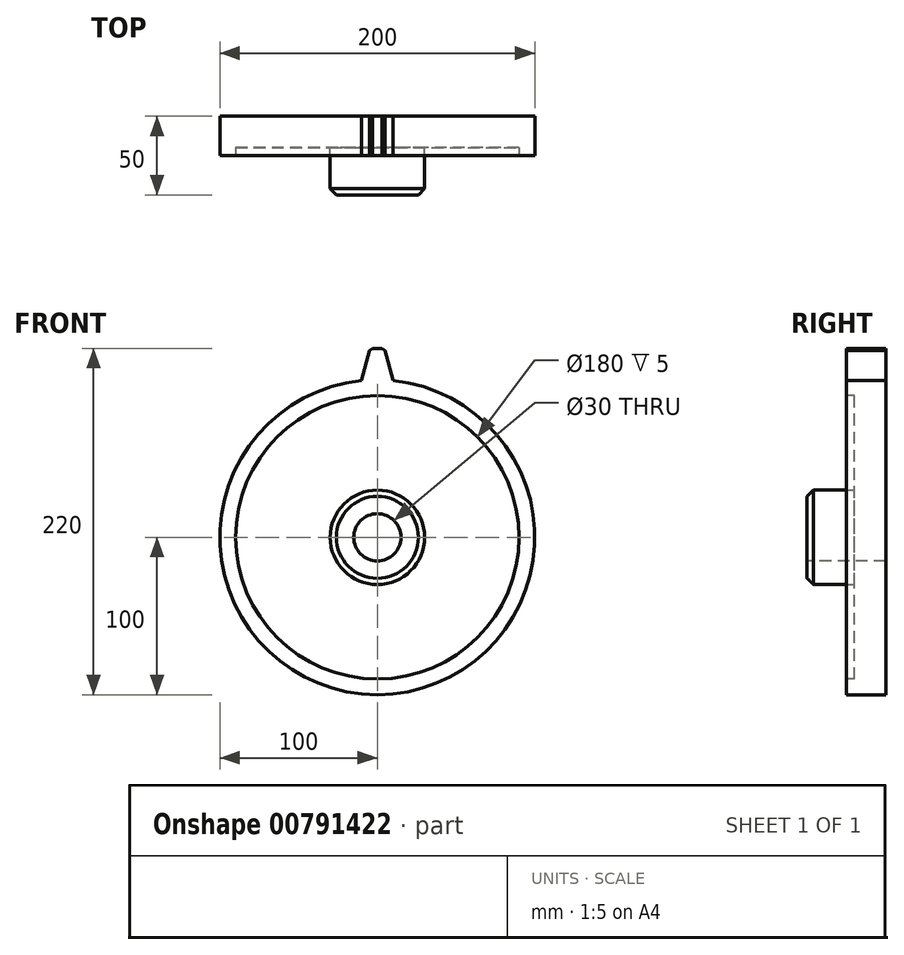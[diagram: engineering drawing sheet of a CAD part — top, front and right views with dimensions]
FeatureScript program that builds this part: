
annotation { "Feature Type Name" : "Feature", "Feature Type Description" : "" }
export const myFeature = defineFeature(function(context is Context, id is Id, definition is map)
    precondition{}
    {
        {
            var Q0;
            Q0=qCreatedBy(makeId("Front.planeOp"),FACE);
            var sketch = newSketch(context, id + "F0", { "sketchPlane" : qUnion([Q0])});
            skCircle(sketch, "E0", {"center": v(0, 0) * mm, "radius": 100 * mm});
            skSolve(sketch);
        }
        {
            var Q0;
            Q0=makeQuery(id+"F0.imprint","IMPRINT",FACE,{"disambiguationData":[TD([[makeQuery(id+"F0.imprint","IMPRINT",EDGE,{"derivedFrom":sQuery(id+"F0.wireOp",EDGE,"E0")}),1.0]])]});
            var Q1;
            Q1 = qSketchRegion(id + "F6", true);
            extrude(context, id + "F1", {"entities" : qUnion([Q0, Q1]), "depth" : 25 * mm, "offsetDistance" : 25 * mm});
        }
        {
            var Q0;
            Q0=makeQuery(id+"F1.opExtrude","CAP_FACE",FACE,{"disambiguationData":[OSD([sQuery(id+"F0.wireOp",EDGE,"E0")])],"isStart":false});
            var sketch = newSketch(context, id + "F2", { "sketchPlane" : qUnion([Q0])});
            skLineSegment(sketch, "E1", {"start": v(-10, 99.5) * mm, "end": v(10, 99.5) * mm});
            skLineSegment(sketch, "E2", {"start": v(10, 99.5) * mm, "end": v(4.5, 120) * mm});
            skLineSegment(sketch, "E3", {"start": v(4.5, 120) * mm, "end": v(-4.5, 120) * mm});
            skLineSegment(sketch, "E4", {"start": v(-4.5, 120) * mm, "end": v(-10, 99.5) * mm});
            skSolve(sketch);
        }
        {
            var Q0;
            {var subQ0=sQuery(id+"F2.wireOp",EDGE,"E2");Q0=makeQuery(id+"F2.imprint","IMPRINT",FACE,{"disambiguationData":[TD([[makeQuery(id+"F2.imprint","IMPRINT",EDGE,{"derivedFrom":subQ0}),1.0]])]});}
            var Q1;
            Q1=makeQuery(id+"F1.opExtrude","CAP_FACE",FACE,{"disambiguationData":[OSD([sQuery(id+"F0.wireOp",EDGE,"E0")])],"isStart":true});
            extrude(context, id + "F3", {"entities" : qUnion([Q0]), "operationType" : NewBodyOperationType.ADD, "endBound" : BoundingType.UP_TO_SURFACE, "oppositeDirection" : true, "depth" : 25 * mm, "endBoundEntityFace" : qUnion([Q1]), "offsetDistance" : 25 * mm});
        }
        {
            var Q0;
            Q0=makeQuery(id+"F3.opExtrude","SWEPT_EDGE",EDGE,{"disambiguationData":[OSD([sQuery(id+"F0.wireOp",EDGE,"E0"),sQuery(id+"F2.wireOp",EDGE,"E1"),sQuery(id+"F2.wireOp",EDGE,"E2")])]});
            var Q1;
            Q1=makeQuery(id+"F3.opExtrude","SWEPT_EDGE",EDGE,{"disambiguationData":[OSD([sQuery(id+"F0.wireOp",EDGE,"E0"),sQuery(id+"F2.wireOp",EDGE,"E1"),sQuery(id+"F2.wireOp",EDGE,"E4")])]});
            fillet(context, id + "F4", {"entities" : qUnion([Q0, Q1]), "radius" : 5 * mm, "tangentPropagation" : true, "allowEdgeOverflow" : false});
        }
        {
            var Q0;
            Q0=makeQuery(id+"F3.opExtrude","SWEPT_EDGE",EDGE,{"disambiguationData":[OSD([sQuery(id+"F2.wireOp",EDGE,"E2"),sQuery(id+"F2.wireOp",EDGE,"E3")])]});
            var Q1;
            Q1=makeQuery(id+"F3.opExtrude","SWEPT_EDGE",EDGE,{"disambiguationData":[OSD([sQuery(id+"F2.wireOp",EDGE,"E3"),sQuery(id+"F2.wireOp",EDGE,"E4")])]});
            chamfer(context, id + "F5", {"entities" : qUnion([Q0, Q1]), "width" : 2 * mm, "tangentPropagation" : true});
        }
        {
            var Q0;
            {var subQ0=sQuery(id+"F2.wireOp",EDGE,"E4");var subQ1=sQuery(id+"F2.wireOp",EDGE,"E3");var subQ2=sQuery(id+"F2.wireOp",EDGE,"E2");var subQ3=sQuery(id+"F0.wireOp",EDGE,"E0");Q0=makeQuery(id+"FVngeMlJqadk3JX_1.19.F3.boolean.opBoolean","MERGE",FACE,{"derivedFrom":[makeQuery(id+"FVngeMlJqadk3JX_1.18.F3.boolean.opBoolean","MERGE",FACE,{"derivedFrom":[makeQuery(id+"FVngeMlJqadk3JX_1.17.F3.boolean.opBoolean","MERGE",FACE,{"derivedFrom":[makeQuery(id+"FVngeMlJqadk3JX_1.16.F3.boolean.opBoolean","MERGE",FACE,{"derivedFrom":[makeQuery(id+"FVngeMlJqadk3JX_1.15.F3.boolean.opBoolean","MERGE",FACE,{"derivedFrom":[makeQuery(id+"FVngeMlJqadk3JX_1.14.F3.boolean.opBoolean","MERGE",FACE,{"derivedFrom":[makeQuery(id+"FVngeMlJqadk3JX_1.13.F3.boolean.opBoolean","MERGE",FACE,{"derivedFrom":[makeQuery(id+"FVngeMlJqadk3JX_1.12.F3.boolean.opBoolean","MERGE",FACE,{"derivedFrom":[makeQuery(id+"FVngeMlJqadk3JX_1.11.F3.boolean.opBoolean","MERGE",FACE,{"derivedFrom":[makeQuery(id+"FVngeMlJqadk3JX_1.10.F3.boolean.opBoolean","MERGE",FACE,{"derivedFrom":[makeQuery(id+"FVngeMlJqadk3JX_1.9.F3.boolean.opBoolean","MERGE",FACE,{"derivedFrom":[makeQuery(id+"FVngeMlJqadk3JX_1.8.F3.boolean.opBoolean","MERGE",FACE,{"derivedFrom":[makeQuery(id+"FVngeMlJqadk3JX_1.7.F3.boolean.opBoolean","MERGE",FACE,{"derivedFrom":[makeQuery(id+"FVngeMlJqadk3JX_1.6.F3.boolean.opBoolean","MERGE",FACE,{"derivedFrom":[makeQuery(id+"FVngeMlJqadk3JX_1.5.F3.boolean.opBoolean","MERGE",FACE,{"derivedFrom":[makeQuery(id+"FVngeMlJqadk3JX_1.4.F3.boolean.opBoolean","MERGE",FACE,{"derivedFrom":[makeQuery(id+"FVngeMlJqadk3JX_1.3.F3.boolean.opBoolean","MERGE",FACE,{"derivedFrom":[makeQuery(id+"FVngeMlJqadk3JX_1.2.F3.boolean.opBoolean","MERGE",FACE,{"derivedFrom":[makeQuery(id+"FVngeMlJqadk3JX_1.1.F3.boolean.opBoolean","MERGE",FACE,{"derivedFrom":[makeQuery(id+"F3.boolean.opBoolean","MERGE",FACE,{"derivedFrom":[makeQuery(id+"F1.opExtrude","CAP_FACE",FACE,{"disambiguationData":[OSD([subQ3])],"isStart":false}),makeQuery(id+"F3.opExtrude","CAP_FACE",FACE,{"disambiguationData":[OSD([subQ3,subQ2,subQ1,subQ0])],"isStart":true})]}),makeQuery(id+"FVngeMlJqadk3JX_1.1.F3.opExtrude","CAP_FACE",FACE,{"disambiguationData":[OSD([subQ3,subQ2,subQ1,subQ0])],"isStart":true})]}),makeQuery(id+"FVngeMlJqadk3JX_1.2.F3.opExtrude","CAP_FACE",FACE,{"disambiguationData":[OSD([subQ3,subQ2,subQ1,subQ0])],"isStart":true})]}),makeQuery(id+"FVngeMlJqadk3JX_1.3.F3.opExtrude","CAP_FACE",FACE,{"disambiguationData":[OSD([subQ3,subQ2,subQ1,subQ0])],"isStart":true})]}),makeQuery(id+"FVngeMlJqadk3JX_1.4.F3.opExtrude","CAP_FACE",FACE,{"disambiguationData":[OSD([subQ3,subQ2,subQ1,subQ0])],"isStart":true})]}),makeQuery(id+"FVngeMlJqadk3JX_1.5.F3.opExtrude","CAP_FACE",FACE,{"disambiguationData":[OSD([subQ3,subQ2,subQ1,subQ0])],"isStart":true})]}),makeQuery(id+"FVngeMlJqadk3JX_1.6.F3.opExtrude","CAP_FACE",FACE,{"disambiguationData":[OSD([subQ3,subQ2,subQ1,subQ0])],"isStart":true})]}),makeQuery(id+"FVngeMlJqadk3JX_1.7.F3.opExtrude","CAP_FACE",FACE,{"disambiguationData":[OSD([subQ3,subQ2,subQ1,subQ0])],"isStart":true})]}),makeQuery(id+"FVngeMlJqadk3JX_1.8.F3.opExtrude","CAP_FACE",FACE,{"disambiguationData":[OSD([subQ3,subQ2,subQ1,subQ0])],"isStart":true})]}),makeQuery(id+"FVngeMlJqadk3JX_1.9.F3.opExtrude","CAP_FACE",FACE,{"disambiguationData":[OSD([subQ3,subQ2,subQ1,subQ0])],"isStart":true})]}),makeQuery(id+"FVngeMlJqadk3JX_1.10.F3.opExtrude","CAP_FACE",FACE,{"disambiguationData":[OSD([subQ3,subQ2,subQ1,subQ0])],"isStart":true})]}),makeQuery(id+"FVngeMlJqadk3JX_1.11.F3.opExtrude","CAP_FACE",FACE,{"disambiguationData":[OSD([subQ3,subQ2,subQ1,subQ0])],"isStart":true})]}),makeQuery(id+"FVngeMlJqadk3JX_1.12.F3.opExtrude","CAP_FACE",FACE,{"disambiguationData":[OSD([subQ3,subQ2,subQ1,subQ0])],"isStart":true})]}),makeQuery(id+"FVngeMlJqadk3JX_1.13.F3.opExtrude","CAP_FACE",FACE,{"disambiguationData":[OSD([subQ3,subQ2,subQ1,subQ0])],"isStart":true})]}),makeQuery(id+"FVngeMlJqadk3JX_1.14.F3.opExtrude","CAP_FACE",FACE,{"disambiguationData":[OSD([subQ3,subQ2,subQ1,subQ0])],"isStart":true})]}),makeQuery(id+"FVngeMlJqadk3JX_1.15.F3.opExtrude","CAP_FACE",FACE,{"disambiguationData":[OSD([subQ3,subQ2,subQ1,subQ0])],"isStart":true})]}),makeQuery(id+"FVngeMlJqadk3JX_1.16.F3.opExtrude","CAP_FACE",FACE,{"disambiguationData":[OSD([subQ3,subQ2,subQ1,subQ0])],"isStart":true})]}),makeQuery(id+"FVngeMlJqadk3JX_1.17.F3.opExtrude","CAP_FACE",FACE,{"disambiguationData":[OSD([subQ3,subQ2,subQ1,subQ0])],"isStart":true})]}),makeQuery(id+"FVngeMlJqadk3JX_1.18.F3.opExtrude","CAP_FACE",FACE,{"disambiguationData":[OSD([subQ3,subQ2,subQ1,subQ0])],"isStart":true})]}),makeQuery(id+"FVngeMlJqadk3JX_1.19.F3.opExtrude","CAP_FACE",FACE,{"disambiguationData":[OSD([subQ3,subQ2,subQ1,subQ0])],"isStart":true})]});}
            var sketch = newSketch(context, id + "F6", { "sketchPlane" : qUnion([Q0])});
            skCircle(sketch, "E5", {"center": v(0, 0) * mm, "radius": 90 * mm});
            skSolve(sketch);
        }
        {
            var Q0;
            Q0=makeQuery(id+"F6.imprint","IMPRINT",FACE,{"disambiguationData":[TD([[makeQuery(id+"F6.imprint","IMPRINT",EDGE,{"derivedFrom":sQuery(id+"F6.wireOp",EDGE,"E5")}),1.0]])]});
            extrude(context, id + "F7", {"entities" : qUnion([Q0]), "operationType" : NewBodyOperationType.REMOVE, "oppositeDirection" : true, "depth" : 5 * mm, "offsetDistance" : 25 * mm});
        }
        {
            var Q0;
            Q0=makeQuery(id+"F7.boolean.opBoolean","COPY",FACE,{"derivedFrom":makeQuery(id+"F7.opExtrude","CAP_FACE",FACE,{"disambiguationData":[OSD([sQuery(id+"F6.wireOp",EDGE,"E5")])],"isStart":false})});
            var sketch = newSketch(context, id + "F8", { "sketchPlane" : qUnion([Q0])});
            skCircle(sketch, "E6", {"center": v(0, 0) * mm, "radius": 30 * mm});
            skSolve(sketch);
        }
        {
            var Q0;
            Q0=makeQuery(id+"F8.imprint","IMPRINT",FACE,{"disambiguationData":[TD([[makeQuery(id+"F8.imprint","IMPRINT",EDGE,{"derivedFrom":sQuery(id+"F8.wireOp",EDGE,"E6")}),1.0]])]});
            extrude(context, id + "F9", {"entities" : qUnion([Q0]), "operationType" : NewBodyOperationType.ADD, "depth" : 30 * mm, "offsetDistance" : 25 * mm});
        }
        {
            var Q0;
            Q0=makeQuery(id+"F9.opExtrude","CAP_FACE",FACE,{"disambiguationData":[OSD([sQuery(id+"F8.wireOp",EDGE,"E6")])],"isStart":false});
            var sketch = newSketch(context, id + "F10", { "sketchPlane" : qUnion([Q0])});
            skCircle(sketch, "E7", {"center": v(0, 0) * mm, "radius": 15 * mm});
            skSolve(sketch);
        }
        {
            var Q0;
            Q0=makeQuery(id+"F10.imprint","IMPRINT",FACE,{"disambiguationData":[TD([[makeQuery(id+"F10.imprint","IMPRINT",EDGE,{"derivedFrom":sQuery(id+"F10.wireOp",EDGE,"E7")}),1.0]])]});
            extrude(context, id + "F11", {"entities" : qUnion([Q0]), "operationType" : NewBodyOperationType.REMOVE, "endBound" : BoundingType.THROUGH_ALL, "oppositeDirection" : true, "depth" : 25 * mm, "offsetDistance" : 25 * mm});
        }
        {
            var Q0;
            Q0=makeQuery(id+"F9.opExtrude","CAP_EDGE",EDGE,{"disambiguationData":[OSD([sQuery(id+"F8.wireOp",EDGE,"E6")])],"isStart":false});
            var Q1;
            Q1=makeQuery(id+"F11.boolean.opBoolean","COPY",EDGE,{"derivedFrom":makeQuery(id+"F11.opExtrude","CAP_EDGE",EDGE,{"disambiguationData":[OSD([sQuery(id+"F10.wireOp",EDGE,"E7")])],"isStart":true})});
            chamfer(context, id + "F12", {"entities" : qUnion([Q0, Q1]), "width" : 4 * mm, "tangentPropagation" : true});
        }
    });
